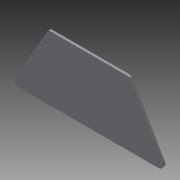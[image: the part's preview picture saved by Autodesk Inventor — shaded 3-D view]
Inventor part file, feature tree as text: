
AUTODESK INVENTOR PART (.ipt)
format: ipt  version: 2015 (Build 190159000, 159)  size: 81,920 bytes
history: native  units: in
note: dims shown in document units (in); Inventor stores cm internally (conversion verified against a paired STEP export)
features: extrude x1, sketch x1
ambient origin geometry x8: Origin, YZ Plane, XZ Plane, XY Plane, X Axis, Y Axis, Z Axis, Center Point
bodies: Solid1 (feature_tree)
feature tree (2):
  extrude  "Extrusion1"  TaperAngle=60.0deg  [1 undecoded]
  sketch  "Sketch1"  dims[d0=75.0deg d1=60.0deg d2=0.25in d3=0.25in d4=0.5in d5=20.0in d9=0.25in d10=0.0in d11=10.0in]
note: 1 required parameter value undecoded (feature->parameter linkage not recoverable at this tier; creation-order binding heuristic only, values carry confidence <= 0.55)
